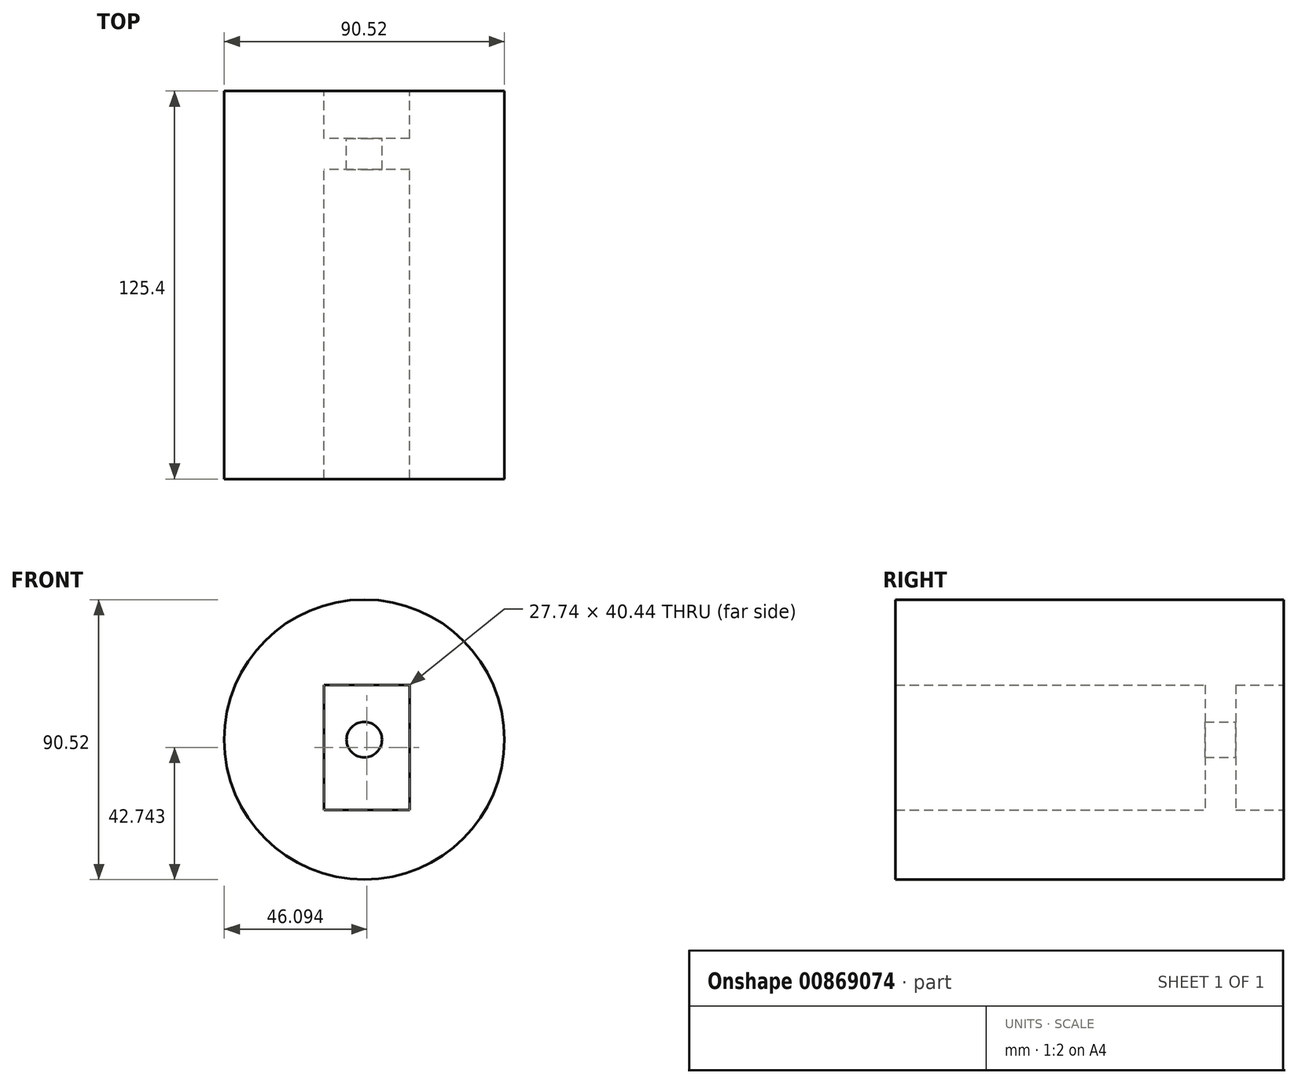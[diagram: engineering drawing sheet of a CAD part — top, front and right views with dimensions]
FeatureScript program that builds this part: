
annotation { "Feature Type Name" : "Feature", "Feature Type Description" : "" }
export const myFeature = defineFeature(function(context is Context, id is Id, definition is map)
    precondition{}
    {
        {
            var Q0;
            Q0=qCreatedBy(makeId("Front.planeOp"),FACE);
            var sketch = newSketch(context, id + "F0", { "sketchPlane" : qUnion([Q0])});
            skCircle(sketch, "E0", {"center": v(0, 0) * mm, "radius": 5.73 * mm});
            skCircle(sketch, "E1", {"center": v(0, 0) * mm, "radius": 45.26 * mm});
            skSolve(sketch);
        }
        {
            var Q0;
            Q0=makeQuery(id+"F0.imprint","IMPRINT",FACE,{"disambiguationData":[TD([[makeQuery(id+"F0.imprint","IMPRINT",EDGE,{"derivedFrom":sQuery(id+"F0.wireOp",EDGE,"E0")}),-1.0]])]});
            extrude(context, id + "F1", {"entities" : qUnion([Q0]), "endBound" : BoundingType.SYMMETRIC, "depth" : 10 * mm, "offsetDistance" : 25.4 * mm});
        }
        {
            var Q0;
            Q0=makeQuery(id+"F1.opExtrude","CAP_FACE",FACE,{"disambiguationData":[OSD([sQuery(id+"F0.wireOp",EDGE,"E0"),sQuery(id+"F0.wireOp",EDGE,"E1")])],"isStart":false});
            var sketch = newSketch(context, id + "F2", { "sketchPlane" : qUnion([Q0])});
            skLineSegment(sketch, "E2.bottom", {"start": v(-13.03, -22.73) * mm, "end": v(14.7, -22.73) * mm});
            skLineSegment(sketch, "E2.top", {"start": v(-13.03, 17.7) * mm, "end": v(14.7, 17.7) * mm});
            skLineSegment(sketch, "E2.left", {"start": v(-13.03, -22.73) * mm, "end": v(-13.03, 17.7) * mm});
            skLineSegment(sketch, "E2.right", {"start": v(14.7, -22.73) * mm, "end": v(14.7, 17.7) * mm});
            skSolve(sketch);
        }
        {
            var Q0;
            Q0=makeQuery(id+"F2.imprint","IMPRINT",FACE,{"disambiguationData":[TD([[makeQuery(id+"F2.imprint","IMPRINT",EDGE,{"derivedFrom":sQuery(id+"F2.wireOp",EDGE,"E2.bottom")}),-1.0]])]});
            extrude(context, id + "F3", {"entities" : qUnion([Q0]), "operationType" : NewBodyOperationType.ADD, "depth" : 100 * mm, "offsetDistance" : 25.4 * mm, "hasSecondDirection" : true, "secondDirectionOppositeDirection" : true, "secondDirectionDepth" : 25.4 * mm});
        }
    });
